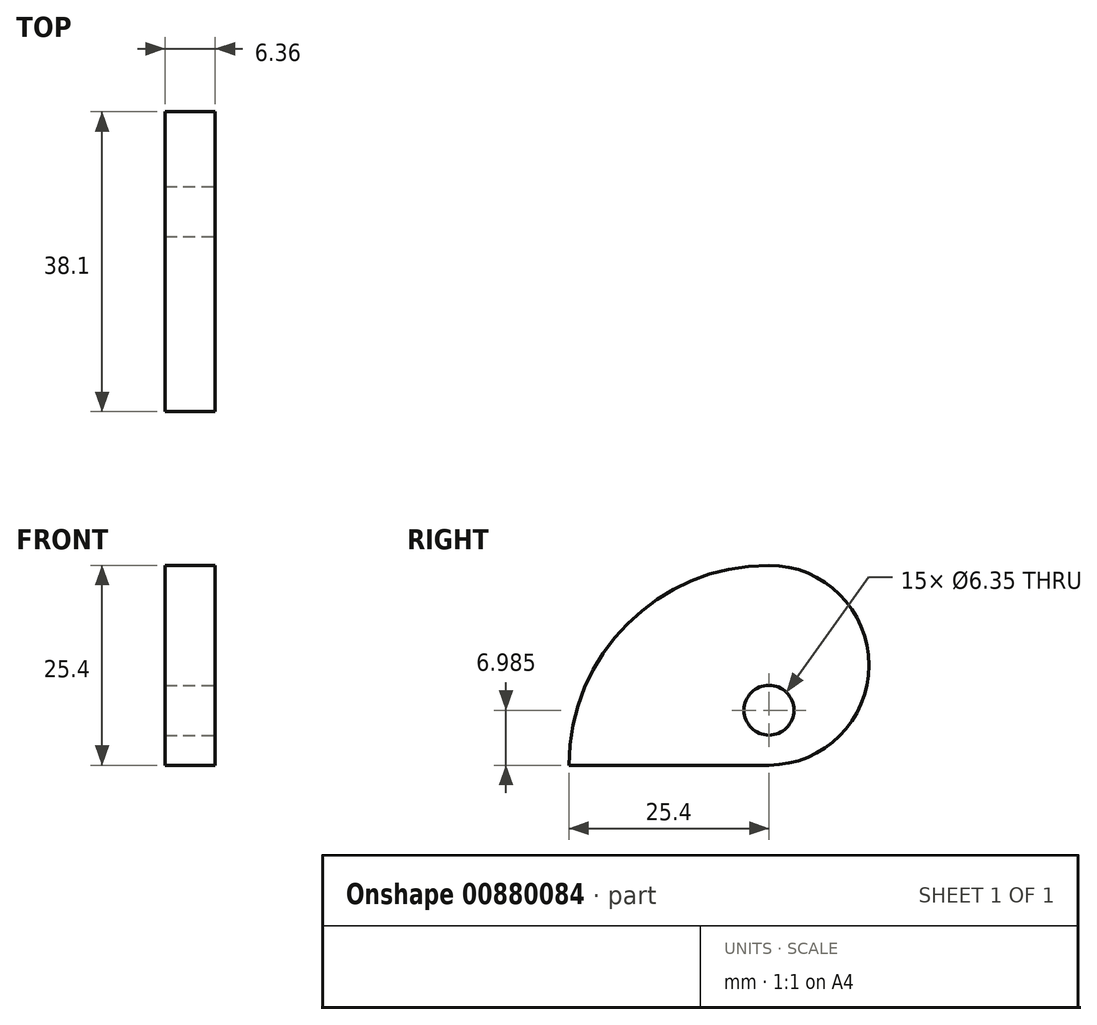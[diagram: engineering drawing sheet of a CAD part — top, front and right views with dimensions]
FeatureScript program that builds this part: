
annotation { "Feature Type Name" : "Feature", "Feature Type Description" : "" }
export const myFeature = defineFeature(function(context is Context, id is Id, definition is map)
    precondition{}
    {
        {
            var Q0;
            Q0=qCreatedBy(makeId("Right.planeOp"),FACE);
            var sketch = newSketch(context, id + "F0", { "sketchPlane" : qUnion([Q0])});
            skLineSegment(sketch, "E0.bottom", {"start": v(0, 0) * mm, "end": v(12.7, 0) * mm});
            skLineSegment(sketch, "E0.top", {"start": v(0, 12.7) * mm, "end": v(12.7, 12.7) * mm});
            skLineSegment(sketch, "E0.left", {"start": v(0, 0) * mm, "end": v(0, 12.7) * mm});
            skLineSegment(sketch, "E0.right", {"start": v(12.7, 0) * mm, "end": v(12.7, 12.7) * mm});
            skLineSegment(sketch, "E1.top", {"start": v(0, -12.7) * mm, "end": v(12.7, -12.7) * mm});
            skLineSegment(sketch, "E1.left", {"start": v(0, 0) * mm, "end": v(0, -12.7) * mm});
            skLineSegment(sketch, "E1.right", {"start": v(12.7, 0) * mm, "end": v(12.7, -12.7) * mm});
            skLineSegment(sketch, "E2.bottom", {"start": v(0, 12.7) * mm, "end": v(-25.4, 12.7) * mm});
            skLineSegment(sketch, "E2.top", {"start": v(0, -12.7) * mm, "end": v(-25.4, -12.7) * mm});
            skLineSegment(sketch, "E2.left", {"start": v(0, 12.7) * mm, "end": v(0, -12.7) * mm});
            skLineSegment(sketch, "E2.right", {"start": v(-25.4, 12.7) * mm, "end": v(-25.4, -12.7) * mm});
            skLineSegment(sketch, "E3.bottom", {"start": v(-25.4, -12.7) * mm, "end": v(12.7, -12.7) * mm});
            skLineSegment(sketch, "E3.top", {"start": v(-25.4, -50.8) * mm, "end": v(12.7, -50.8) * mm});
            skLineSegment(sketch, "E3.left", {"start": v(-25.4, -12.7) * mm, "end": v(-25.4, -50.8) * mm});
            skLineSegment(sketch, "E3.right", {"start": v(12.7, -12.7) * mm, "end": v(12.7, -50.8) * mm});
            skLineSegment(sketch, "E4.bottom", {"start": v(12.7, 12.7) * mm, "end": v(76.2, 12.7) * mm});
            skLineSegment(sketch, "E4.top", {"start": v(12.7, -50.8) * mm, "end": v(76.2, -50.8) * mm});
            skLineSegment(sketch, "E4.left", {"start": v(12.7, 12.7) * mm, "end": v(12.7, -50.8) * mm});
            skLineSegment(sketch, "E4.right", {"start": v(76.2, 12.7) * mm, "end": v(76.2, -50.8) * mm});
            skLineSegment(sketch, "E5.bottom", {"start": v(-25.4, 12.7) * mm, "end": v(76.2, 12.7) * mm});
            skLineSegment(sketch, "E5.top", {"start": v(-25.4, 114.3) * mm, "end": v(76.2, 114.3) * mm});
            skLineSegment(sketch, "E5.left", {"start": v(-25.4, 12.7) * mm, "end": v(-25.4, 114.3) * mm});
            skLineSegment(sketch, "E5.right", {"start": v(76.2, 12.7) * mm, "end": v(76.2, 114.3) * mm});
            skLineSegment(sketch, "E6.bottom", {"start": v(-25.4, 114.3) * mm, "end": v(-190.5, 114.3) * mm});
            skLineSegment(sketch, "E6.top", {"start": v(-25.4, -50.8) * mm, "end": v(-190.5, -50.8) * mm});
            skLineSegment(sketch, "E6.left", {"start": v(-25.4, 114.3) * mm, "end": v(-25.4, -50.8) * mm});
            skLineSegment(sketch, "E6.right", {"start": v(-190.5, 114.3) * mm, "end": v(-190.5, -50.8) * mm});
            skArc(sketch, "E7", {"start": v(0, -12.7) * mm, "mid": v(8.98, -8.98) * mm, "end": v(12.7, 0) * mm});
            skArc(sketch, "E8", {"start": v(12.7, 0) * mm, "mid": v(8.98, 8.98) * mm, "end": v(0, 12.7) * mm});
            skArc(sketch, "E9", {"start": v(0, 12.7) * mm, "mid": v(-17.96, 5.26) * mm, "end": v(-25.4, -12.7) * mm});
            skArc(sketch, "E10", {"start": v(-25.4, -12.7) * mm, "mid": v(-14.24, -39.64) * mm, "end": v(12.7, -50.8) * mm});
            skArc(sketch, "E11", {"start": v(12.7, -50.8) * mm, "mid": v(57.6, -32.2) * mm, "end": v(76.2, 12.7) * mm});
            skArc(sketch, "E12", {"start": v(76.2, 12.7) * mm, "mid": v(46.44, 84.54) * mm, "end": v(-25.4, 114.3) * mm});
            skArc(sketch, "E13", {"start": v(-25.4, 114.3) * mm, "mid": v(-142.14, 65.94) * mm, "end": v(-190.5, -50.8) * mm});
            skSolve(sketch);
        }
        {
            var Q0;
            Q0=makeQuery(id+"F0.imprint","IMPRINT",FACE,{"disambiguationData":[TD([[makeQuery(id+"F0.imprint","IMPRINT",EDGE,{"derivedFrom":sQuery(id+"F0.wireOp",EDGE,"E0.left")}),1.0]])]});
            var Q1;
            Q1=makeQuery(id+"F0.imprint","IMPRINT",FACE,{"disambiguationData":[TD([[makeQuery(id+"F0.imprint","IMPRINT",EDGE,{"derivedFrom":sQuery(id+"F0.wireOp",EDGE,"E0.bottom")}),1.0]])]});
            var Q2;
            Q2=makeQuery(id+"F0.imprint","IMPRINT",FACE,{"disambiguationData":[TD([[makeQuery(id+"F0.imprint","IMPRINT",EDGE,{"derivedFrom":sQuery(id+"F0.wireOp",EDGE,"E0.bottom")}),-1.0]])]});
            extrude(context, id + "F1", {"entities" : qUnion([Q0, Q1, Q2]), "endBound" : BoundingType.SYMMETRIC, "depth" : 6.35 * mm, "offsetDistance" : 25.4 * mm});
        }
        {
            var Q0;
            Q0=makeQuery(id+"F1.opExtrude","CAP_FACE",FACE,{"disambiguationData":[OSD([sQuery(id+"F0.wireOp",EDGE,"E2.top"),sQuery(id+"F0.wireOp",EDGE,"E7"),sQuery(id+"F0.wireOp",EDGE,"E8"),sQuery(id+"F0.wireOp",EDGE,"E9")])],"isStart":false});
            var sketch = newSketch(context, id + "F2", { "sketchPlane" : qUnion([Q0])});
            skCircle(sketch, "E14", {"center": v(0, -5.72) * mm, "radius": 3.18 * mm});
            skSolve(sketch);
        }
        {
            var Q0;
            Q0=makeQuery(id+"F2.imprint","IMPRINT",FACE,{"disambiguationData":[TD([[makeQuery(id+"F2.imprint","IMPRINT",EDGE,{"derivedFrom":sQuery(id+"F2.wireOp",EDGE,"E14")}),1.0]])]});
            extrude(context, id + "F3", {"entities" : qUnion([Q0]), "operationType" : NewBodyOperationType.REMOVE, "endBound" : BoundingType.THROUGH_ALL, "oppositeDirection" : true, "depth" : 25.4 * mm, "offsetDistance" : 25.4 * mm});
        }
    });
